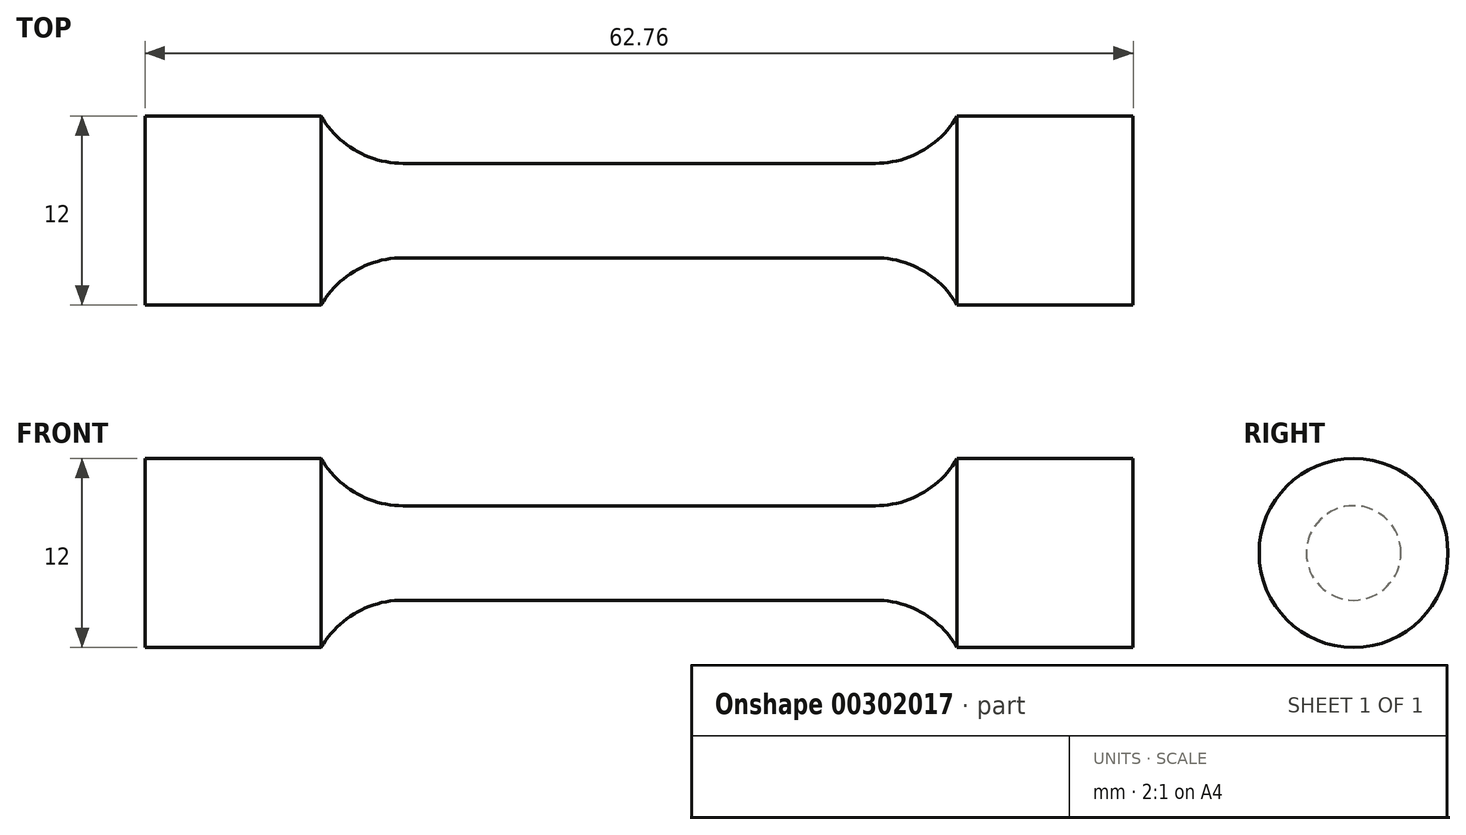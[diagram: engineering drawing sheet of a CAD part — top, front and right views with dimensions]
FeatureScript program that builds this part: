
annotation { "Feature Type Name" : "Feature", "Feature Type Description" : "" }
export const myFeature = defineFeature(function(context is Context, id is Id, definition is map)
    precondition{}
    {
        {
            var Q0;
            Q0=qCreatedBy(makeId("Front.planeOp"),FACE);
            var sketch = newSketch(context, id + "F0", { "sketchPlane" : qUnion([Q0])});
            skLineSegment(sketch, "E0", {"start": v(-33.4, 0) * mm, "end": v(40.08, 0) * mm, "construction": true});
            skLineSegment(sketch, "E1", {"start": v(0, 28.1) * mm, "end": v(0, -22.78) * mm, "construction": true});
            skLineSegment(sketch, "E2", {"start": v(-15, 3) * mm, "end": v(15, 3) * mm});
            skLineSegment(sketch, "E3", {"start": v(-31.38, 6) * mm, "end": v(-20.2, 6) * mm});
            skPoint(sketch, "E4", {"position": v(0, 6) * mm});
            skPoint(sketch, "E5", {"position": v(0, 3) * mm});
            skArc(sketch, "E6", {"start": v(15, 3) * mm, "mid": v(18, 3.8) * mm, "end": v(20.2, 6) * mm});
            skLineSegment(sketch, "E7", {"start": v(31.38, 6) * mm, "end": v(31.38, 0) * mm});
            skLineSegment(sketch, "E8.MirrorCS", {"start": v(-31.38, 6) * mm, "end": v(-31.38, 0) * mm});
            skArc(sketch, "E9.MirrorCS", {"start": v(-15, 3) * mm, "mid": v(-18, 3.8) * mm, "end": v(-20.2, 6) * mm});
            skLineSegment(sketch, "E10", {"start": v(-31.38, 0) * mm, "end": v(31.38, 0) * mm});
            skLineSegment(sketch, "E11.trimOffspring", {"start": v(20.2, 6) * mm, "end": v(31.38, 6) * mm});
            skSolve(sketch);
        }
        {
            var Q0;
            Q0=qSketchRegion(id+"F0",true);
            var Q1;
            Q1=sQuery(id+"F0.wireOp",EDGE,"E10");
            revolve(context, id + "F1", {"entities" : qUnion([Q0]), "axis" : qUnion([Q1]), "revolveType" : RevolveType.FULL});
        }
    });
